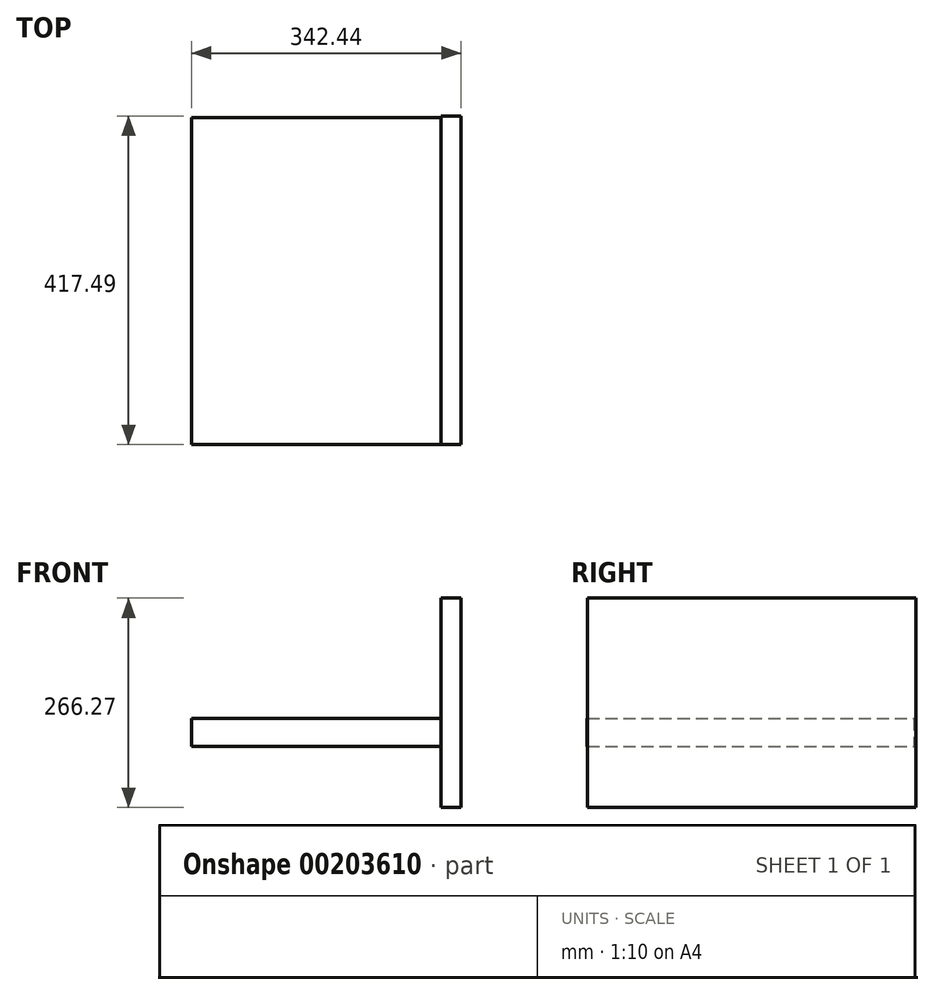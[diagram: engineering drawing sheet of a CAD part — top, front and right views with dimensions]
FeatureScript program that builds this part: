
annotation { "Feature Type Name" : "Feature", "Feature Type Description" : "" }
export const myFeature = defineFeature(function(context is Context, id is Id, definition is map)
    precondition{}
    {
        {
            var Q0;
            Q0=qCreatedBy(makeId("Right.planeOp"),FACE);
            var sketch = newSketch(context, id + "F0", { "sketchPlane" : qUnion([Q0])});
            skLineSegment(sketch, "E0.bottom", {"start": v(0, -77.5) * mm, "end": v(-236.2, -77.5) * mm});
            skLineSegment(sketch, "E0.top", {"start": v(0, 188.77) * mm, "end": v(-236.2, 188.77) * mm});
            skLineSegment(sketch, "E0.left", {"start": v(0, -77.5) * mm, "end": v(0, 188.77) * mm});
            skLineSegment(sketch, "E0.right", {"start": v(-236.2, -77.5) * mm, "end": v(-236.2, 188.77) * mm});
            skLineSegment(sketch, "E1.bottom", {"start": v(0, -77.5) * mm, "end": v(180.95, -77.5) * mm});
            skLineSegment(sketch, "E1.top", {"start": v(0, 188.77) * mm, "end": v(180.95, 188.77) * mm});
            skLineSegment(sketch, "E1.right", {"start": v(180.95, -77.5) * mm, "end": v(180.95, 188.77) * mm});
            skSolve(sketch);
        }
        {
            var Q0;
            Q0 = qSketchRegion(id + "F0", true);
            extrude(context, id + "F1", {"entities" : qUnion([Q0]), "depth" : 25.4 * mm});
        }
        {
            var Q0;
            Q0=qCreatedBy(makeId("Top.planeOp"),FACE);
            var sketch = newSketch(context, id + "F2", { "sketchPlane" : qUnion([Q0])});
            skLineSegment(sketch, "E2.bottom", {"start": v(0, -236.54) * mm, "end": v(-317.04, -236.54) * mm});
            skLineSegment(sketch, "E2.top", {"start": v(0, 178.76) * mm, "end": v(-317.04, 178.76) * mm});
            skLineSegment(sketch, "E2.left", {"start": v(0, -236.54) * mm, "end": v(0, 178.76) * mm});
            skLineSegment(sketch, "E2.right", {"start": v(-317.04, -236.54) * mm, "end": v(-317.04, 178.76) * mm});
            skSolve(sketch);
        }
        {
            var Q0;
            Q0 = qSketchRegion(id + "F2", true);
            extrude(context, id + "F3", {"entities" : qUnion([Q0]), "operationType" : NewBodyOperationType.ADD, "depth" : 35.56 * mm});
        }
    });
